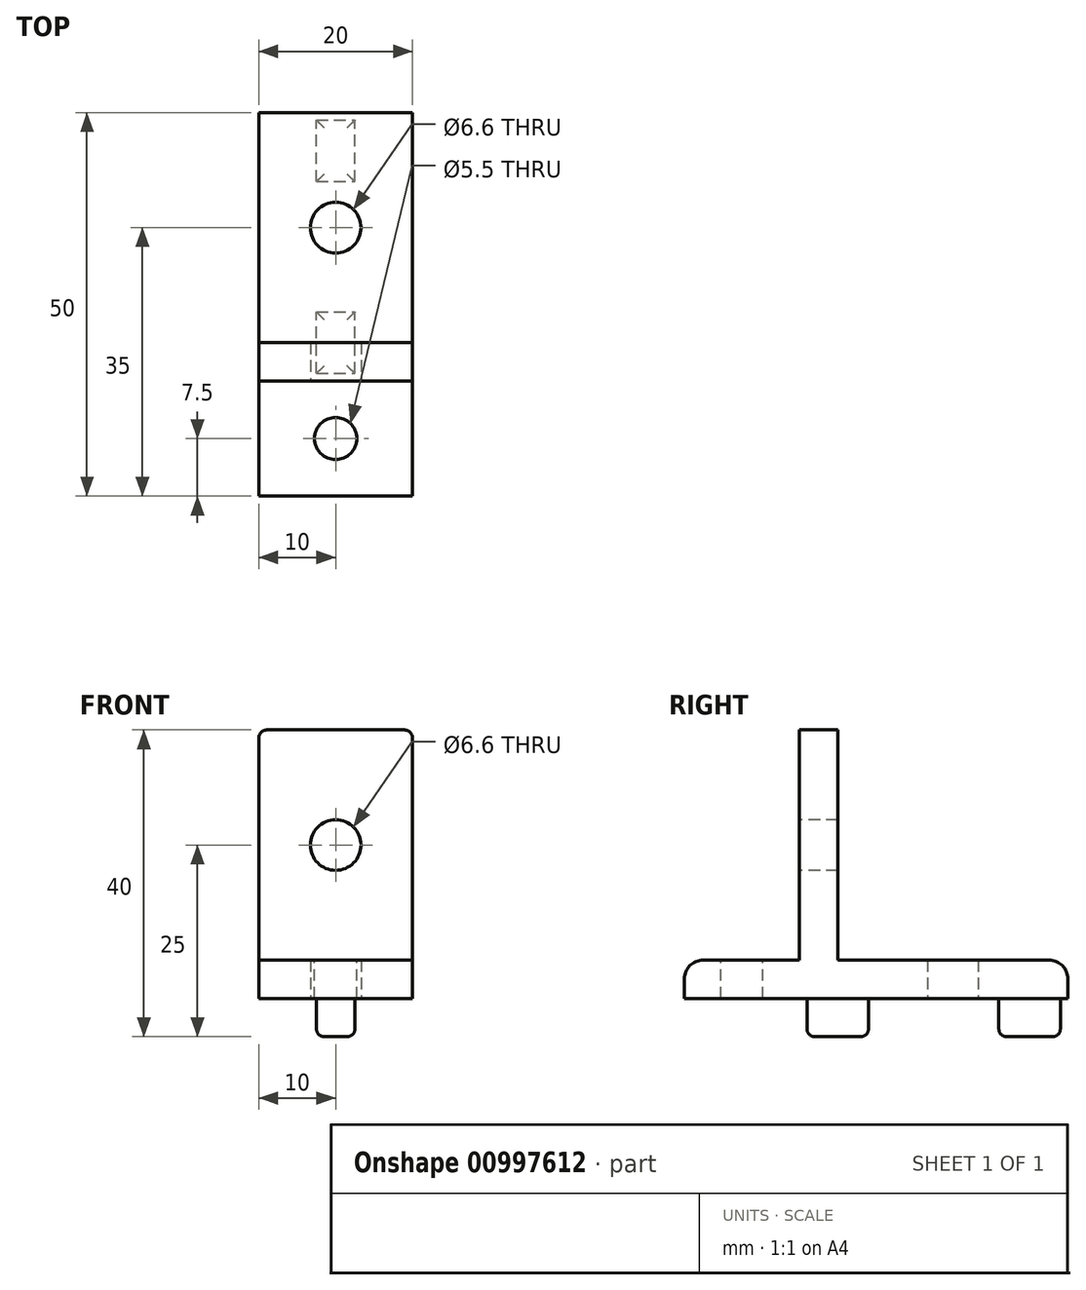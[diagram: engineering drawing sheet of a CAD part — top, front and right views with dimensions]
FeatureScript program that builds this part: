
annotation { "Feature Type Name" : "Feature", "Feature Type Description" : "" }
export const myFeature = defineFeature(function(context is Context, id is Id, definition is map)
    precondition{}
    {
        {
            var Q0;
            Q0=qCreatedBy(makeId("Top.planeOp"),FACE);
            var sketch = newSketch(context, id + "F0", { "sketchPlane" : qUnion([Q0])});
            skLineSegment(sketch, "E0.bottom", {"start": v(10, 25) * mm, "end": v(-10, 25) * mm});
            skLineSegment(sketch, "E0.top", {"start": v(10, -25) * mm, "end": v(-10, -25) * mm});
            skLineSegment(sketch, "E0.left", {"start": v(10, 25) * mm, "end": v(10, -25) * mm});
            skLineSegment(sketch, "E0.right", {"start": v(-10, 25) * mm, "end": v(-10, -25) * mm});
            skPoint(sketch, "E0.middle", {"position": v(0, 0) * mm});
            skSolve(sketch);
        }
        {
            var Q0;
            Q0=makeQuery(id+"F0.imprint","IMPRINT",FACE,{"disambiguationData":[TD([[makeQuery(id+"F0.imprint","IMPRINT",EDGE,{"derivedFrom":sQuery(id+"F0.wireOp",EDGE,"E0.bottom")}),1.0]])]});
            extrude(context, id + "F1", {"entities" : qUnion([Q0]), "depth" : 5 * mm, "offsetDistance" : 25 * mm});
        }
        {
            var Q0;
            Q0=makeQuery(id+"F1.opExtrude","CAP_FACE",FACE,{"disambiguationData":[OSD([sQuery(id+"F0.wireOp",EDGE,"E0.bottom"),sQuery(id+"F0.wireOp",EDGE,"E0.top"),sQuery(id+"F0.wireOp",EDGE,"E0.left"),sQuery(id+"F0.wireOp",EDGE,"E0.right")])],"isStart":true});
            var sketch = newSketch(context, id + "F2", { "sketchPlane" : qUnion([Q0])});
            skLineSegment(sketch, "E1.bottom", {"start": v(-2.5, -16) * mm, "end": v(2.5, -16) * mm});
            skLineSegment(sketch, "E1.top", {"start": v(-2.5, -24) * mm, "end": v(2.5, -24) * mm});
            skLineSegment(sketch, "E1.left", {"start": v(-2.5, -16) * mm, "end": v(-2.5, -24) * mm});
            skLineSegment(sketch, "E1.right", {"start": v(2.5, -16) * mm, "end": v(2.5, -24) * mm});
            skPoint(sketch, "E1.middle", {"position": v(0, -20) * mm});
            skLineSegment(sketch, "E2.bottom", {"start": v(-2.5, 9) * mm, "end": v(2.5, 9) * mm});
            skLineSegment(sketch, "E2.top", {"start": v(-2.5, 1) * mm, "end": v(2.5, 1) * mm});
            skLineSegment(sketch, "E2.left", {"start": v(-2.5, 9) * mm, "end": v(-2.5, 1) * mm});
            skLineSegment(sketch, "E2.right", {"start": v(2.5, 9) * mm, "end": v(2.5, 1) * mm});
            skPoint(sketch, "E2.middle", {"position": v(0, 5) * mm});
            skSolve(sketch);
        }
        {
            var Q0;
            Q0=makeQuery(id+"F2.imprint","IMPRINT",FACE,{"disambiguationData":[TD([[makeQuery(id+"F2.imprint","IMPRINT",EDGE,{"derivedFrom":sQuery(id+"F2.wireOp",EDGE,"E1.bottom")}),-1.0]])]});
            var Q1;
            Q1=makeQuery(id+"F2.imprint","IMPRINT",FACE,{"disambiguationData":[TD([[makeQuery(id+"F2.imprint","IMPRINT",EDGE,{"derivedFrom":sQuery(id+"F2.wireOp",EDGE,"E2.bottom")}),-1.0]])]});
            extrude(context, id + "F3", {"entities" : qUnion([Q0, Q1]), "operationType" : NewBodyOperationType.ADD, "depth" : 5 * mm, "offsetDistance" : 25 * mm});
        }
        {
            var Q0;
            Q0=makeQuery(id+"F3.opExtrude","CAP_EDGE",EDGE,{"disambiguationData":[OSD([sQuery(id+"F2.wireOp",EDGE,"E1.right")])],"isStart":false});
            var Q1;
            Q1=makeQuery(id+"F3.opExtrude","CAP_EDGE",EDGE,{"disambiguationData":[OSD([sQuery(id+"F2.wireOp",EDGE,"E1.left")])],"isStart":false});
            var Q2;
            Q2=makeQuery(id+"F3.opExtrude","CAP_EDGE",EDGE,{"disambiguationData":[OSD([sQuery(id+"F2.wireOp",EDGE,"E1.top")])],"isStart":false});
            var Q3;
            Q3=makeQuery(id+"F3.opExtrude","CAP_EDGE",EDGE,{"disambiguationData":[OSD([sQuery(id+"F2.wireOp",EDGE,"E1.bottom")])],"isStart":false});
            var Q4;
            Q4=makeQuery(id+"F3.opExtrude","CAP_EDGE",EDGE,{"disambiguationData":[OSD([sQuery(id+"F2.wireOp",EDGE,"E2.top")])],"isStart":false});
            var Q5;
            Q5=makeQuery(id+"F3.opExtrude","CAP_EDGE",EDGE,{"disambiguationData":[OSD([sQuery(id+"F2.wireOp",EDGE,"E2.left")])],"isStart":false});
            var Q6;
            Q6=makeQuery(id+"F3.opExtrude","CAP_EDGE",EDGE,{"disambiguationData":[OSD([sQuery(id+"F2.wireOp",EDGE,"E2.bottom")])],"isStart":false});
            var Q7;
            Q7=makeQuery(id+"F3.opExtrude","CAP_EDGE",EDGE,{"disambiguationData":[OSD([sQuery(id+"F2.wireOp",EDGE,"E2.right")])],"isStart":false});
            fillet(context, id + "F4", {"entities" : qUnion([Q0, Q1, Q2, Q3, Q4, Q5, Q6, Q7]), "radius" : 1 * mm, "tangentPropagation" : true, "allowEdgeOverflow" : false});
        }
        {
            var Q0;
            Q0=makeQuery(id+"F1.opExtrude","CAP_FACE",FACE,{"disambiguationData":[OSD([sQuery(id+"F0.wireOp",EDGE,"E0.bottom"),sQuery(id+"F0.wireOp",EDGE,"E0.top"),sQuery(id+"F0.wireOp",EDGE,"E0.left"),sQuery(id+"F0.wireOp",EDGE,"E0.right")])],"isStart":true});
            var sketch = newSketch(context, id + "F5", { "sketchPlane" : qUnion([Q0])});
            skPoint(sketch, "E3", {"position": v(0, -10) * mm});
            skSolve(sketch);
        }
        {
            var Q0;
            Q0=sQuery(id+"F5.wireOp",VERTEX,"E3");
            var Q1;
            Q1=makeQuery(id+"F1.opExtrude","SWEPT_BODY",BODY,{"disambiguationData":[OSD([sQuery(id+"F0.wireOp",EDGE,"E0.bottom"),sQuery(id+"F0.wireOp",EDGE,"E0.top"),sQuery(id+"F0.wireOp",EDGE,"E0.left"),sQuery(id+"F0.wireOp",EDGE,"E0.right")])]});
            hole(context, id + "F6", {"style" : HoleStyle.SIMPLE, "endStyle" : HoleEndStyle.THROUGH, "standardTappedOrClearance" : lookupTablePath({ "fit" : "Normal", "standard" : "ISO", "size" : "M6", "type" : "Clearance" }), "standardBlindInLast" : lookupTablePath({ "fit" : "Normal", "standard" : "ISO", "engagement" : "75%", "pitch" : "1 mm", "size" : "M6", "type" : "Clearance & tapped" }), "holeDiameter" : 6.6 * mm, "majorDiameter" : 5 * mm, "isTappedThrough" : true, "tappedDepth" : 9 * mm, "tapClearance" : 2, "locations" : qUnion([Q0]), "scope" : qUnion([Q1])});
        }
        {
            var Q0;
            Q0=makeQuery(id+"F1.opExtrude","CAP_FACE",FACE,{"disambiguationData":[OSD([sQuery(id+"F0.wireOp",EDGE,"E0.bottom"),sQuery(id+"F0.wireOp",EDGE,"E0.top"),sQuery(id+"F0.wireOp",EDGE,"E0.left"),sQuery(id+"F0.wireOp",EDGE,"E0.right")])],"isStart":false});
            var sketch = newSketch(context, id + "F7", { "sketchPlane" : qUnion([Q0])});
            skLineSegment(sketch, "E4", {"start": v(-10, -5) * mm, "end": v(10, -5) * mm});
            skLineSegment(sketch, "E5", {"start": v(-10, -5) * mm, "end": v(-10, -10) * mm});
            skLineSegment(sketch, "E6", {"start": v(-10, -10) * mm, "end": v(10, -10) * mm});
            skLineSegment(sketch, "E7", {"start": v(10, -10) * mm, "end": v(10, -5) * mm});
            skSolve(sketch);
        }
        {
            var Q0;
            Q0=makeQuery(id+"F7.imprint","IMPRINT",FACE,{"disambiguationData":[TD([[makeQuery(id+"F7.imprint","IMPRINT",EDGE,{"derivedFrom":sQuery(id+"F7.wireOp",EDGE,"E4")}),-1.0]])]});
            extrude(context, id + "F8", {"entities" : qUnion([Q0]), "operationType" : NewBodyOperationType.ADD, "depth" : 30 * mm, "offsetDistance" : 25 * mm});
        }
        {
            var Q0;
            Q0=makeQuery(id+"F8.opExtrude","CAP_EDGE",EDGE,{"disambiguationData":[OSD([sQuery(id+"F7.wireOp",EDGE,"E7")])],"isStart":false});
            var Q1;
            Q1=makeQuery(id+"F8.opExtrude","CAP_EDGE",EDGE,{"disambiguationData":[OSD([sQuery(id+"F7.wireOp",EDGE,"E5")])],"isStart":false});
            fillet(context, id + "F9", {"entities" : qUnion([Q0, Q1]), "radius" : 1 * mm, "tangentPropagation" : true, "allowEdgeOverflow" : false});
        }
        {
            var Q0;
            Q0=makeQuery(id+"F8.opExtrude","SWEPT_FACE",FACE,{"disambiguationData":[OSD([sQuery(id+"F7.wireOp",EDGE,"E6")])]});
            var sketch = newSketch(context, id + "F10", { "sketchPlane" : qUnion([Q0])});
            skPoint(sketch, "E8", {"position": v(0, 20) * mm});
            skPoint(sketch, "E8.positionSnap0", {"position": v(0, 5) * mm});
            skSolve(sketch);
        }
        {
            var Q0;
            Q0=sQuery(id+"F10.wireOp",VERTEX,"E8");
            var Q1;
            Q1=makeQuery(id+"F1.opExtrude","SWEPT_BODY",BODY,{"disambiguationData":[OSD([sQuery(id+"F0.wireOp",EDGE,"E0.bottom"),sQuery(id+"F0.wireOp",EDGE,"E0.top"),sQuery(id+"F0.wireOp",EDGE,"E0.left"),sQuery(id+"F0.wireOp",EDGE,"E0.right")])]});
            hole(context, id + "F11", {"style" : HoleStyle.SIMPLE, "endStyle" : HoleEndStyle.THROUGH, "standardTappedOrClearance" : lookupTablePath({ "fit" : "Normal", "standard" : "ISO", "size" : "M6", "type" : "Clearance" }), "standardBlindInLast" : lookupTablePath({ "fit" : "Normal", "standard" : "ISO", "engagement" : "75%", "pitch" : "1 mm", "size" : "M6", "type" : "Clearance & tapped" }), "holeDiameter" : 6.6 * mm, "majorDiameter" : 5 * mm, "isTappedThrough" : true, "tappedDepth" : 9 * mm, "tapClearance" : 2, "locations" : qUnion([Q0]), "scope" : qUnion([Q1])});
        }
        {
            var Q0;
            {var subQ0=sQuery(id+"F0.wireOp",EDGE,"E0.right");var subQ1=sQuery(id+"F0.wireOp",EDGE,"E0.left");var subQ2=sQuery(id+"F0.wireOp",EDGE,"E0.top");Q0=makeQuery(id+"F8.boolean.opBoolean","SPLIT",FACE,{"disambiguationData":[TD([makeQuery(id+"F1.opExtrude","SWEPT_FACE",FACE,{"disambiguationData":[OSD([subQ2])]})])],"derivedFrom":makeQuery(id+"F1.opExtrude","CAP_FACE",FACE,{"disambiguationData":[OSD([sQuery(id+"F0.wireOp",EDGE,"E0.bottom"),subQ2,subQ1,subQ0])],"isStart":false})});}
            var sketch = newSketch(context, id + "F12", { "sketchPlane" : qUnion([Q0])});
            skPoint(sketch, "E9", {"position": v(0, -17.5) * mm});
            skPoint(sketch, "E9.positionSnap0", {"position": v(0, -10) * mm});
            skSolve(sketch);
        }
        {
            var Q0;
            Q0=sQuery(id+"F12.wireOp",VERTEX,"E9");
            var Q1;
            Q1=makeQuery(id+"F1.opExtrude","SWEPT_BODY",BODY,{"disambiguationData":[OSD([sQuery(id+"F0.wireOp",EDGE,"E0.bottom"),sQuery(id+"F0.wireOp",EDGE,"E0.top"),sQuery(id+"F0.wireOp",EDGE,"E0.left"),sQuery(id+"F0.wireOp",EDGE,"E0.right")])]});
            hole(context, id + "F13", {"style" : HoleStyle.SIMPLE, "endStyle" : HoleEndStyle.THROUGH, "standardTappedOrClearance" : lookupTablePath({ "fit" : "Normal", "standard" : "ISO", "size" : "M5", "type" : "Clearance" }), "standardBlindInLast" : lookupTablePath({ "fit" : "Normal", "standard" : "ISO", "engagement" : "75%", "pitch" : "0.8 mm", "size" : "M5", "type" : "Clearance & tapped" }), "holeDiameter" : 5.5 * mm, "majorDiameter" : 5 * mm, "isTappedThrough" : true, "tappedDepth" : 9 * mm, "tapClearance" : 2, "locations" : qUnion([Q0]), "scope" : qUnion([Q1])});
        }
        {
            var Q0;
            Q0=makeQuery(id+"F1.opExtrude","CAP_EDGE",EDGE,{"disambiguationData":[OSD([sQuery(id+"F0.wireOp",EDGE,"E0.bottom")])],"isStart":false});
            var Q1;
            Q1=makeQuery(id+"F1.opExtrude","CAP_EDGE",EDGE,{"disambiguationData":[OSD([sQuery(id+"F0.wireOp",EDGE,"E0.top")])],"isStart":false});
            fillet(context, id + "F14", {"entities" : qUnion([Q0, Q1]), "radius" : 2.5 * mm, "tangentPropagation" : true, "allowEdgeOverflow" : false});
        }
    });
